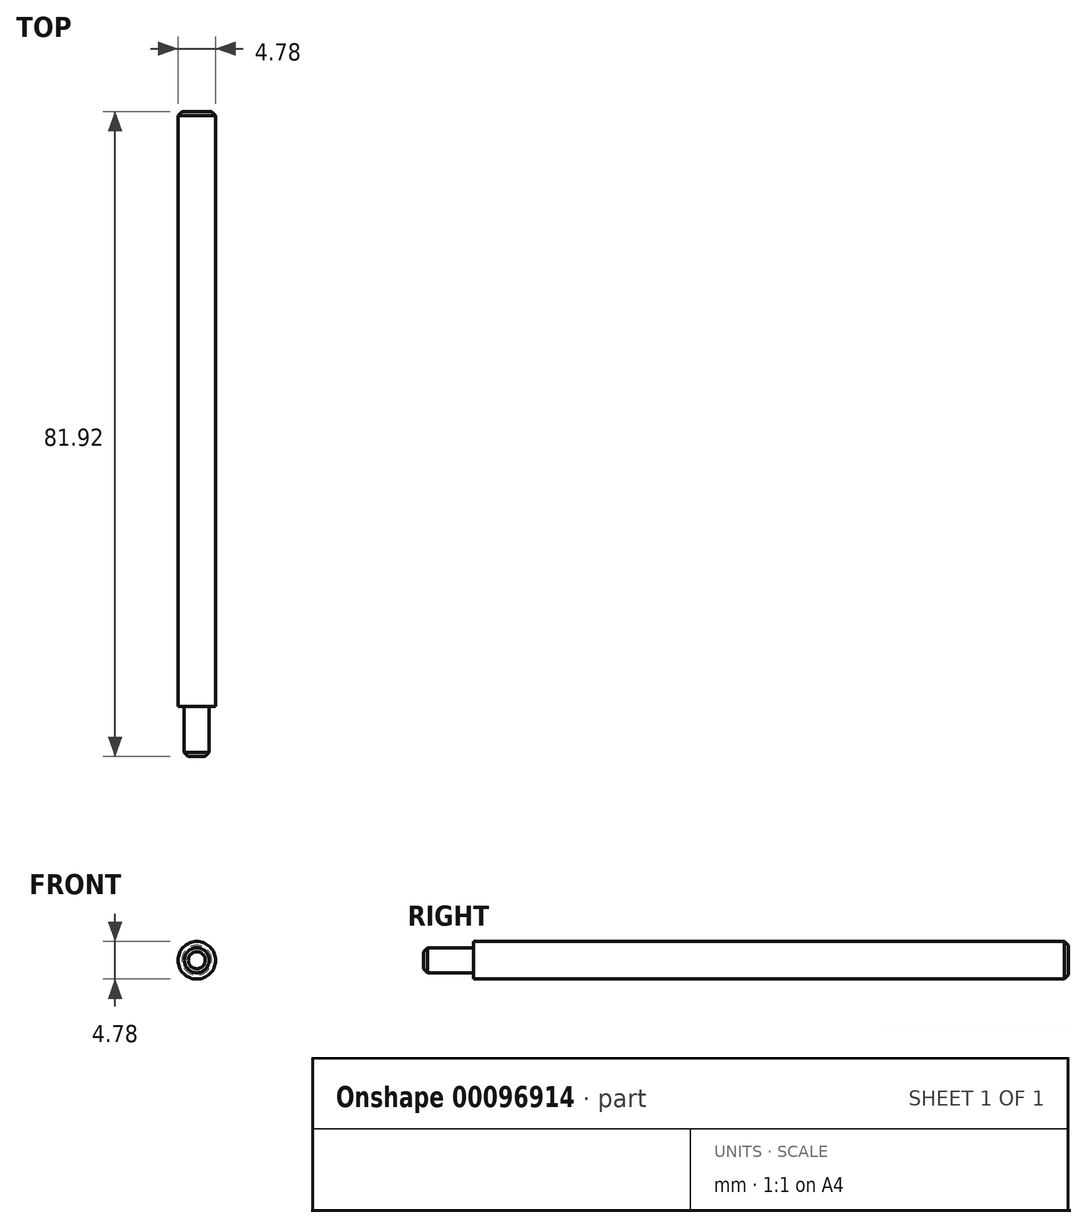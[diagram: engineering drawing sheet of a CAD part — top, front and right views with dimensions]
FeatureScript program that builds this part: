
annotation { "Feature Type Name" : "Feature", "Feature Type Description" : "" }
export const myFeature = defineFeature(function(context is Context, id is Id, definition is map)
    precondition{}
    {
        {
            var Q0;
            Q0=qCreatedBy(makeId("Front.planeOp"),FACE);
            var sketch = newSketch(context, id + "F0", { "sketchPlane" : qUnion([Q0])});
            skCircle(sketch, "E0", {"center": v(0, 0) * mm, "radius": 2.39 * mm});
            skSolve(sketch);
        }
        {
            var Q0;
            Q0=makeQuery(id+"F0.imprint","IMPRINT",FACE,{"disambiguationData":[TD([[makeQuery(id+"F0.imprint","IMPRINT",EDGE,{"derivedFrom":sQuery(id+"F0.wireOp",EDGE,"E0")}),1.0]])]});
            extrude(context, id + "F1", {"entities" : qUnion([Q0]), "depth" : 75.56 * mm});
        }
        {
            var Q0;
            Q0=makeQuery(id+"F1.opExtrude","CAP_FACE",FACE,{"disambiguationData":[OSD([sQuery(id+"F0.wireOp",EDGE,"E0")])],"isStart":false});
            var sketch = newSketch(context, id + "F2", { "sketchPlane" : qUnion([Q0])});
            skCircle(sketch, "E1", {"center": v(0, 0) * mm, "radius": 1.59 * mm});
            skSolve(sketch);
        }
        {
            var Q0;
            Q0=makeQuery(id+"F2.imprint","IMPRINT",FACE,{"disambiguationData":[TD([[makeQuery(id+"F2.imprint","IMPRINT",EDGE,{"derivedFrom":sQuery(id+"F2.wireOp",EDGE,"E1")}),1.0]])]});
            extrude(context, id + "F3", {"entities" : qUnion([Q0]), "operationType" : NewBodyOperationType.ADD, "depth" : 6.35 * mm});
        }
        {
            var Q0;
            Q0=makeQuery(id+"F3.opExtrude","CAP_EDGE",EDGE,{"disambiguationData":[OSD([sQuery(id+"F2.wireOp",EDGE,"E1")])],"isStart":false});
            var Q1;
            Q1=makeQuery(id+"F1.opExtrude","CAP_EDGE",EDGE,{"disambiguationData":[OSD([sQuery(id+"F0.wireOp",EDGE,"E0")])],"isStart":true});
            chamfer(context, id + "F4", {"entities" : qUnion([Q0, Q1]), "width" : 0.5 * mm, "tangentPropagation" : true});
        }
    });
